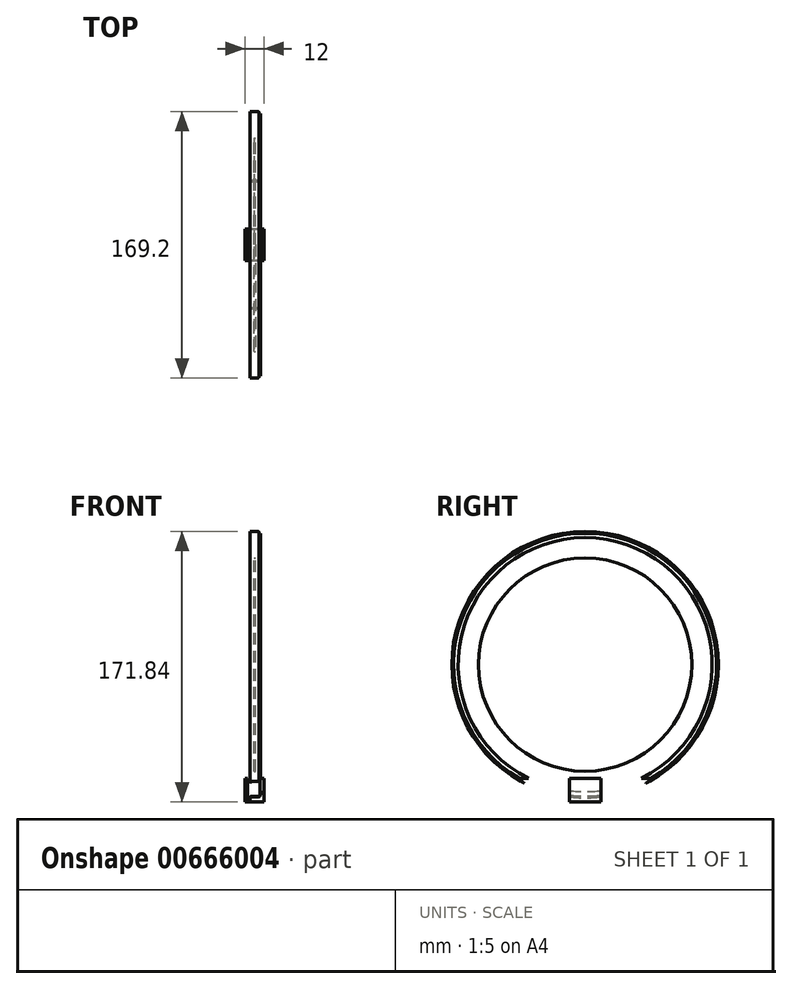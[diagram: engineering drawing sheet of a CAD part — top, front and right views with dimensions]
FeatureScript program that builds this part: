
annotation { "Feature Type Name" : "Feature", "Feature Type Description" : "" }
export const myFeature = defineFeature(function(context is Context, id is Id, definition is map)
    precondition{}
    {
        {
            var Q0;
            Q0=qCreatedBy(makeId("Top.planeOp"),FACE);
            cPlane(context, id + "F0", {"entities" : qUnion([Q0]), "cplaneType" : CPlaneType.OFFSET, "offset" : 87.24 * mm, "oppositeDirection" : true, "width" : 150 * mm, "height" : 150 * mm});
        }
        {
            var Q0;
            Q0=qCreatedBy(id+"F0.planeOp",FACE);
            var sketch = newSketch(context, id + "F1", { "sketchPlane" : qUnion([Q0])});
            skLineSegment(sketch, "E0.bottom", {"start": v(7.5, 40) * mm, "end": v(-7.5, 40) * mm});
            skLineSegment(sketch, "E0.top", {"start": v(7.5, -40) * mm, "end": v(-7.5, -40) * mm});
            skLineSegment(sketch, "E0.left", {"start": v(7.5, 40) * mm, "end": v(7.5, -40) * mm});
            skLineSegment(sketch, "E0.right", {"start": v(-7.5, 40) * mm, "end": v(-7.5, -40) * mm});
            skPoint(sketch, "E0.middle", {"position": v(0, 0) * mm});
            skSolve(sketch);
        }
        {
            var Q0;
            Q0 = qSketchRegion(id + "F1", true);
            extrude(context, id + "F2", {"entities" : qUnion([Q0]), "depth" : 15 * mm, "offsetDistance" : 25 * mm});
        }
        {
            var Q0;
            Q0=qCreatedBy(makeId("Front.planeOp"),FACE);
            var sketch = newSketch(context, id + "F3", { "sketchPlane" : qUnion([Q0])});
            skLineSegment(sketch, "E1", {"start": v(-0.85, 0) * mm, "end": v(0, 0) * mm});
            skLineSegment(sketch, "E2.MirrorCS", {"start": v(0.5, -79.5) * mm, "end": v(1.25, -79.5) * mm});
            skLineSegment(sketch, "E3.MirrorCS", {"start": v(-3.9, -86.5) * mm, "end": v(-3.9, -85.1) * mm});
            skLineSegment(sketch, "E4.MirrorCS", {"start": v(-4.75, -86.5) * mm, "end": v(-3.9, -86.5) * mm});
            skLineSegment(sketch, "E5.MirrorCS", {"start": v(-4.75, -86.5) * mm, "end": v(-4.75, -84.75) * mm});
            skLineSegment(sketch, "E6.MirrorCS", {"start": v(-3.75, -83.75) * mm, "end": v(1.14, -83.75) * mm});
            skLineSegment(sketch, "E7.MirrorCS", {"start": v(1.16, -80.35) * mm, "end": v(0.15, -80.35) * mm});
            skLineSegment(sketch, "E8.MirrorCS", {"start": v(2.4, -82.49) * mm, "end": v(2.4, -81.6) * mm});
            skLineSegment(sketch, "E9.MirrorCS", {"start": v(3.25, -81.5) * mm, "end": v(3.25, -82.6) * mm});
            skLineSegment(sketch, "E10.MirrorCS", {"start": v(-3.4, -84.6) * mm, "end": v(1.25, -84.6) * mm});
            skLineSegment(sketch, "E11.MirrorCS", {"start": v(0, 0) * mm, "end": v(0, -79) * mm});
            skLineSegment(sketch, "E12.MirrorCS", {"start": v(-0.85, -79.35) * mm, "end": v(-0.85, 0) * mm});
            skPoint(sketch, "E13.visualSharp", {"position": v(3.25, -79.5) * mm});
            skArc(sketch, "E13.filletArc", {"start": v(3.25, -81.5) * mm, "mid": v(2.66, -80.09) * mm, "end": v(1.25, -79.5) * mm});
            skPoint(sketch, "E14.visualSharp", {"position": v(2.4, -80.35) * mm});
            skArc(sketch, "E14.filletArc", {"start": v(2.4, -81.6) * mm, "mid": v(2.04, -80.71) * mm, "end": v(1.16, -80.35) * mm});
            skPoint(sketch, "E15.visualSharp", {"position": v(2.4, -83.75) * mm});
            skArc(sketch, "E15.filletArc", {"start": v(1.14, -83.75) * mm, "mid": v(2.03, -83.38) * mm, "end": v(2.4, -82.49) * mm});
            skPoint(sketch, "E16.visualSharp", {"position": v(3.25, -84.6) * mm});
            skArc(sketch, "E16.filletArc", {"start": v(1.25, -84.6) * mm, "mid": v(2.66, -84.01) * mm, "end": v(3.25, -82.6) * mm});
            skPoint(sketch, "E17.visualSharp", {"position": v(-3.9, -84.6) * mm});
            skArc(sketch, "E17.filletArc", {"start": v(-3.4, -84.6) * mm, "mid": v(-3.75, -84.75) * mm, "end": v(-3.9, -85.1) * mm});
            skPoint(sketch, "E18.visualSharp", {"position": v(-4.75, -83.75) * mm});
            skArc(sketch, "E18.filletArc", {"start": v(-3.75, -83.75) * mm, "mid": v(-4.46, -84.04) * mm, "end": v(-4.75, -84.75) * mm});
            skPoint(sketch, "E19.visualSharp", {"position": v(0, -79.5) * mm});
            skArc(sketch, "E19.filletArc", {"start": v(0, -79) * mm, "mid": v(0.15, -79.35) * mm, "end": v(0.5, -79.5) * mm});
            skPoint(sketch, "E20.visualSharp", {"position": v(-0.85, -80.35) * mm});
            skArc(sketch, "E20.filletArc", {"start": v(-0.85, -79.35) * mm, "mid": v(-0.56, -80.06) * mm, "end": v(0.15, -80.35) * mm});
            skSolve(sketch);
        }
        {
            var Q0;
            Q0 = qSketchRegion(id + "F3", true);
            var Q1;
            Q1=sQuery(id+"F3.wireOp",EDGE,"E1");
            revolve(context, id + "F4", {"entities" : qUnion([Q0]), "axis" : qUnion([Q1]), "revolveType" : RevolveType.FULL});
        }
        {
            var Q0;
            Q0=qCreatedBy(makeId("Front.planeOp"),FACE);
            var sketch = newSketch(context, id + "F5", { "sketchPlane" : qUnion([Q0])});
            skLineSegment(sketch, "E21.0", {"start": v(-3.9, -86.5) * mm, "end": v(-3.9, -84.6) * mm, "construction": true});
            skLineSegment(sketch, "E22.0", {"start": v(-4.75, -86.5) * mm, "end": v(-4.75, -67.95) * mm, "construction": true});
            skLineSegment(sketch, "E23.0", {"start": v(-4.75, -86.5) * mm, "end": v(-3.9, -86.5) * mm, "construction": true});
            skLineSegment(sketch, "E24.0", {"start": v(-3.9, -84.6) * mm, "end": v(3.25, -84.6) * mm, "construction": true});
            skLineSegment(sketch, "E25", {"start": v(3.25, -84.6) * mm, "end": v(3.25, -67.95) * mm, "construction": true});
            skLineSegment(sketch, "E26", {"start": v(3.25, -67.95) * mm, "end": v(-4.75, -67.95) * mm, "construction": true});
            skPoint(sketch, "E27.orphan", {"position": v(-4.75, -84.75) * mm});
            skLineSegment(sketch, "E28.0", {"start": v(-3.3, -86.85) * mm, "end": v(-3.3, -84.25) * mm});
            skLineSegment(sketch, "E28.1", {"start": v(-4.95, -86.85) * mm, "end": v(-3.3, -86.85) * mm});
            skLineSegment(sketch, "E28.3", {"start": v(3.05, -84.25) * mm, "end": v(3.05, -67.75) * mm});
            skLineSegment(sketch, "E28.4", {"start": v(3.05, -67.75) * mm, "end": v(-4.95, -67.75) * mm});
            skLineSegment(sketch, "E28.6", {"start": v(-4.95, -86.85) * mm, "end": v(-4.95, -67.75) * mm});
            skLineSegment(sketch, "E29", {"start": v(-3.3, -84.25) * mm, "end": v(3.05, -84.25) * mm});
            skSolve(sketch);
        }
        {
            var Q0;
            Q0 = qSketchRegion(id + "F5", true);
            var Q1;
            Q1=sQuery(id+"F3.wireOp",EDGE,"E1");
            revolve(context, id + "F6", {"operationType" : NewBodyOperationType.REMOVE, "entities" : qUnion([Q0]), "axis" : qUnion([Q1]), "revolveType" : RevolveType.FULL, "oppositeDirection" : true});
        }
        {
            var Q0;
            Q0=makeQuery(id+"F6.boolean.opBoolean","COPY",EDGE,{"derivedFrom":makeQuery(id+"F6.opRevolve","SWEPT_EDGE",EDGE,{"disambiguationData":[OSD([sQuery(id+"F5.wireOp",EDGE,"E28.0"),sQuery(id+"F5.wireOp",EDGE,"E29")])]})});
            fillet(context, id + "F7", {"entities" : qUnion([Q0]), "radius" : 1 * mm, "tangentPropagation" : true, "allowEdgeOverflow" : false});
        }
        {
            var Q0;
            Q0=makeQuery(id+"F4.opRevolve","SWEPT_FACE",FACE,{"disambiguationData":[OSD([sQuery(id+"F3.wireOp",EDGE,"E12.MirrorCS")])]});
            extrude(context, id + "F8", {"entities" : qUnion([Q0]), "operationType" : NewBodyOperationType.REMOVE, "depth" : 25 * mm, "offsetDistance" : 25 * mm});
        }
        {
            var Q0;
            Q0=makeQuery(id+"F4.opRevolve","SWEPT_FACE",FACE,{"disambiguationData":[OSD([sQuery(id+"F3.wireOp",EDGE,"E11.MirrorCS")])]});
            extrude(context, id + "F9", {"entities" : qUnion([Q0]), "operationType" : NewBodyOperationType.REMOVE, "depth" : 25 * mm, "offsetDistance" : 25 * mm});
        }
        {
            var Q0;
            Q0=makeQuery(id+"F2.opExtrude","SWEPT_FACE",FACE,{"disambiguationData":[OSD([sQuery(id+"F1.wireOp",EDGE,"E0.top")])]});
            var Q1;
            Q1=makeQuery(id+"F2.opExtrude","SWEPT_FACE",FACE,{"disambiguationData":[OSD([sQuery(id+"F1.wireOp",EDGE,"E0.bottom")])]});
            extrude(context, id + "F10", {"entities" : qUnion([Q0, Q1]), "operationType" : NewBodyOperationType.REMOVE, "oppositeDirection" : true, "depth" : 30 * mm, "offsetDistance" : 25 * mm, "hasSecondDirection" : true, "secondDirectionOppositeDirection" : false, "secondDirectionDepth" : 30 * mm});
        }
        {
            var Q0;
            Q0=makeQuery(id+"F2.opExtrude","SWEPT_FACE",FACE,{"disambiguationData":[OSD([sQuery(id+"F1.wireOp",EDGE,"E0.left")])]});
            extrude(context, id + "F11", {"entities" : qUnion([Q0]), "operationType" : NewBodyOperationType.REMOVE, "oppositeDirection" : true, "depth" : 2 * mm, "offsetDistance" : 25 * mm});
        }
        {
            var Q0;
            Q0=makeQuery(id+"F2.opExtrude","SWEPT_FACE",FACE,{"disambiguationData":[OSD([sQuery(id+"F1.wireOp",EDGE,"E0.right")])]});
            extrude(context, id + "F12", {"entities" : qUnion([Q0]), "operationType" : NewBodyOperationType.REMOVE, "oppositeDirection" : true, "depth" : 1 * mm, "offsetDistance" : 25 * mm});
        }
    });
